# Revit family: Haworth_Belong_Tool_ReferenceShelfBlotter
name_source: partatom
category: Furniture Systems
revit_build: Autodesk Revit 2018 (Build: 20170223_1515(x64)
units: mm (PartAtom-declared; Revit-internal decimal feet)

## family parameters
Always vertical = Yes
Cut with Voids When Loaded = No
OmniClass Number = 23.40.70.14.64.21
OmniClass Title = Systems Furniture
Part Type = Normal
Room Calculation Point = No
Round Connector Dimension = Use Diameter
Shared = No
Work Plane-Based = No

## types (1)
- Shelf
    Actual Depth = 5"
    Actual Height = 9 7/8"
    Actual Width = 11 5/8"
    Assembly Code = E2020200
    Description = "Haworth - Belong Tools - Reference Shelf Blotter"
    Manufacturer = Haworth
    Model = Haworth - Belong Tools - Reference Shelf Blotter
    Product Page URL = http://www.haworth.com
    Revision Number = 2
    Shelf Finish = Haworth _ Paint _ Graphite
    Size = Verify Final Dim. w/ Haworth
    Sustainability Info = https://www.haworth.com
    URL = www.haworth.com
    Warranty = http://www.haworth.com

## geometry (parser evidence)
native form markers: Sweep x3
no freeform markers — native parametric forms only
